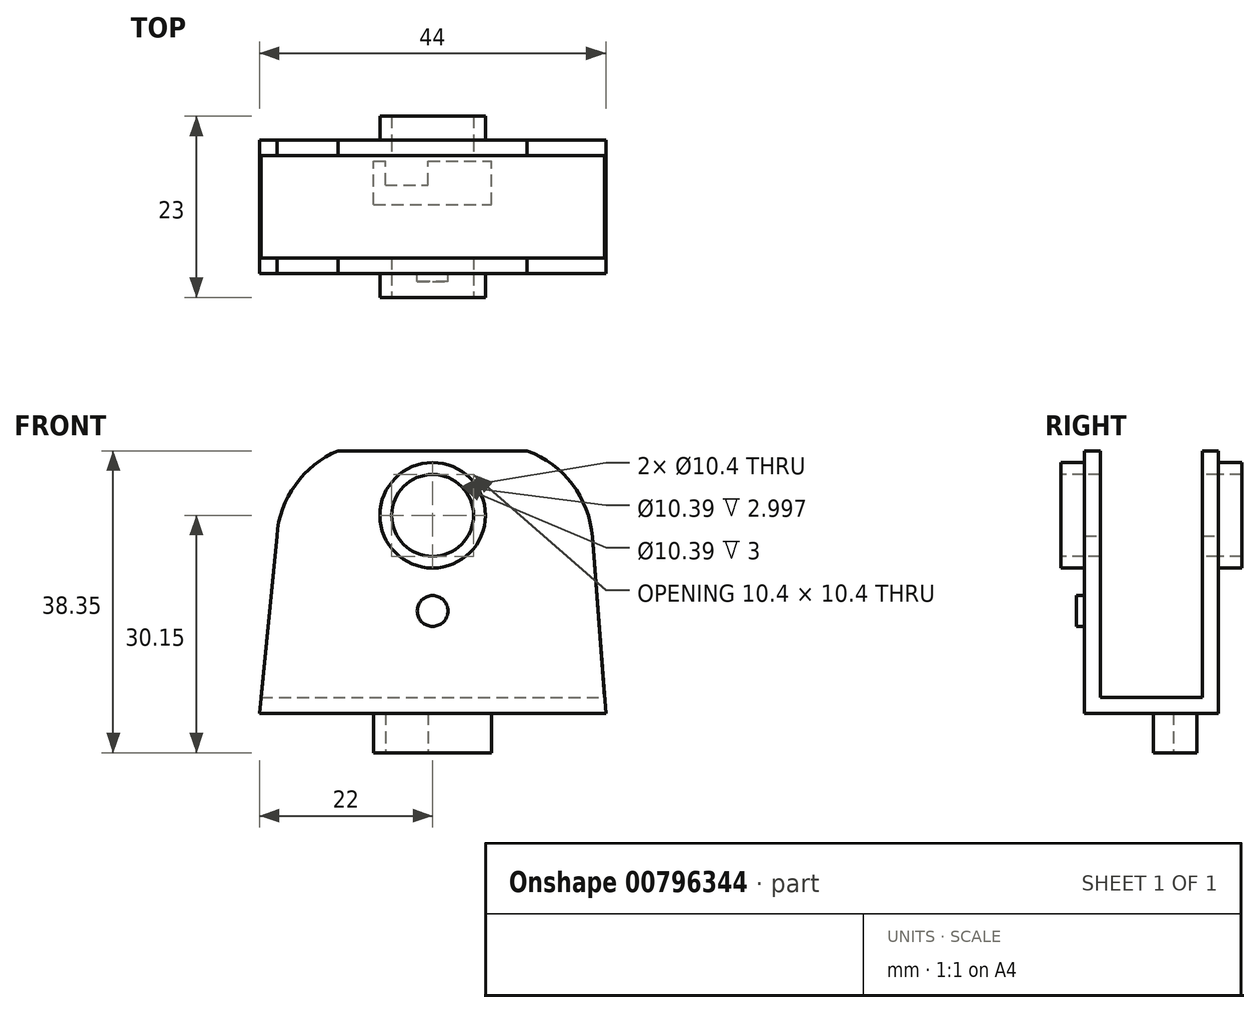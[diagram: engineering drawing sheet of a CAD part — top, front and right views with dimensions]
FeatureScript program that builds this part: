
annotation { "Feature Type Name" : "Feature", "Feature Type Description" : "" }
export const myFeature = defineFeature(function(context is Context, id is Id, definition is map)
    precondition{}
    {
        {
            var Q0;
            Q0=qCreatedBy(makeId("Front.planeOp"),FACE);
            var sketch = newSketch(context, id + "F0", { "sketchPlane" : qUnion([Q0])});
            skLineSegment(sketch, "E0", {"start": v(-22, 0) * mm, "end": v(22, 0) * mm});
            skLineSegment(sketch, "E1", {"start": v(22, 0) * mm, "end": v(20.28, 22.4) * mm});
            skArc(sketch, "E2", {"start": v(20.28, 22.4) * mm, "mid": v(17.75, 29.09) * mm, "end": v(12, 33.35) * mm});
            skLineSegment(sketch, "E3", {"start": v(12, 33.35) * mm, "end": v(-12, 33.35) * mm});
            skArc(sketch, "E4", {"start": v(-12, 33.35) * mm, "mid": v(-17.43, 29.04) * mm, "end": v(-19.79, 22.51) * mm});
            skLineSegment(sketch, "E5", {"start": v(-19.79, 22.51) * mm, "end": v(-22, 0) * mm});
            skSolve(sketch);
        }
        {
            var Q0;
            Q0 = qSketchRegion(id + "F0", true);
            extrude(context, id + "F1", {"entities" : qUnion([Q0]), "depth" : 17 * mm, "offsetDistance" : 25.4 * mm});
        }
        {
            var Q0;
            Q0=qCreatedBy(makeId("Right.planeOp"),FACE);
            var sketch = newSketch(context, id + "F2", { "sketchPlane" : qUnion([Q0])});
            skLineSegment(sketch, "E6.bottom", {"start": v(-15, 2) * mm, "end": v(-2, 2) * mm});
            skLineSegment(sketch, "E6.top", {"start": v(-15, 34.4) * mm, "end": v(-2, 34.4) * mm});
            skLineSegment(sketch, "E6.left", {"start": v(-15, 2) * mm, "end": v(-15, 34.4) * mm});
            skLineSegment(sketch, "E6.right", {"start": v(-2, 2) * mm, "end": v(-2, 34.4) * mm});
            skSolve(sketch);
        }
        {
            var Q0;
            Q0=makeQuery(id+"F2.imprint","IMPRINT",FACE,{"disambiguationData":[TD([[makeQuery(id+"F2.imprint","IMPRINT",EDGE,{"derivedFrom":sQuery(id+"F2.wireOp",EDGE,"E6.bottom")}),1.0]])]});
            extrude(context, id + "F3", {"entities" : qUnion([Q0]), "operationType" : NewBodyOperationType.REMOVE, "endBound" : BoundingType.SYMMETRIC, "oppositeDirection" : true, "depth" : 127 * mm, "offsetDistance" : 25.4 * mm});
        }
        {
            var Q0;
            Q0=makeQuery(id+"F1.opExtrude","CAP_FACE",FACE,{"disambiguationData":[OSD([sQuery(id+"F0.wireOp",EDGE,"E0"),sQuery(id+"F0.wireOp",EDGE,"E1"),sQuery(id+"F0.wireOp",EDGE,"E2"),sQuery(id+"F0.wireOp",EDGE,"E3"),sQuery(id+"F0.wireOp",EDGE,"E4"),sQuery(id+"F0.wireOp",EDGE,"E5")])],"isStart":false});
            var sketch = newSketch(context, id + "F4", { "sketchPlane" : qUnion([Q0])});
            skCircle(sketch, "E7", {"center": v(0, 25.15) * mm, "radius": 5.2 * mm});
            skSolve(sketch);
        }
        {
            var Q0;
            Q0 = qSketchRegion(id + "F4", true);
            extrude(context, id + "F5", {"entities" : qUnion([Q0]), "operationType" : NewBodyOperationType.REMOVE, "endBound" : BoundingType.THROUGH_ALL, "oppositeDirection" : true, "depth" : 25.4 * mm, "offsetDistance" : 25.4 * mm});
        }
        {
            var Q0;
            Q0=makeQuery(id+"F1.opExtrude","CAP_FACE",FACE,{"disambiguationData":[OSD([sQuery(id+"F0.wireOp",EDGE,"E0"),sQuery(id+"F0.wireOp",EDGE,"E1"),sQuery(id+"F0.wireOp",EDGE,"E2"),sQuery(id+"F0.wireOp",EDGE,"E3"),sQuery(id+"F0.wireOp",EDGE,"E4"),sQuery(id+"F0.wireOp",EDGE,"E5")])],"isStart":false});
            var sketch = newSketch(context, id + "F6", { "sketchPlane" : qUnion([Q0])});
            skCircle(sketch, "E8", {"center": v(0, 25.15) * mm, "radius": 6.7 * mm});
            skSolve(sketch);
        }
        {
            var Q0;
            Q0 = qSketchRegion(id + "F6", true);
            extrude(context, id + "F7", {"entities" : qUnion([Q0]), "operationType" : NewBodyOperationType.ADD, "depth" : 3 * mm, "offsetDistance" : 25.4 * mm});
        }
        {
            var Q0;
            Q0=makeQuery(id+"F1.opExtrude","CAP_FACE",FACE,{"disambiguationData":[OSD([sQuery(id+"F0.wireOp",EDGE,"E0"),sQuery(id+"F0.wireOp",EDGE,"E1"),sQuery(id+"F0.wireOp",EDGE,"E2"),sQuery(id+"F0.wireOp",EDGE,"E3"),sQuery(id+"F0.wireOp",EDGE,"E4"),sQuery(id+"F0.wireOp",EDGE,"E5")])],"isStart":true});
            var sketch = newSketch(context, id + "F8", { "sketchPlane" : qUnion([Q0])});
            skCircle(sketch, "E9", {"center": v(0, 25.15) * mm, "radius": 6.7 * mm});
            skSolve(sketch);
        }
        {
            var Q0;
            Q0 = qSketchRegion(id + "F8", true);
            extrude(context, id + "F9", {"entities" : qUnion([Q0]), "operationType" : NewBodyOperationType.ADD, "depth" : 3 * mm, "offsetDistance" : 25.4 * mm});
        }
        {
            var Q0;
            Q0=makeQuery(id+"F7.opExtrude","CAP_FACE",FACE,{"disambiguationData":[OSD([sQuery(id+"F6.wireOp",EDGE,"E8")])],"isStart":false});
            var sketch = newSketch(context, id + "F10", { "sketchPlane" : qUnion([Q0])});
            skCircle(sketch, "E10", {"center": v(0, 25.15) * mm, "radius": 5.2 * mm});
            skSolve(sketch);
        }
        {
            var Q0;
            Q0 = qSketchRegion(id + "F10", true);
            extrude(context, id + "F11", {"entities" : qUnion([Q0]), "operationType" : NewBodyOperationType.REMOVE, "endBound" : BoundingType.THROUGH_ALL, "oppositeDirection" : true, "depth" : 25.4 * mm, "offsetDistance" : 25.4 * mm});
        }
        {
            var Q0;
            Q0=makeQuery(id+"F1.opExtrude","SWEPT_FACE",FACE,{"disambiguationData":[OSD([sQuery(id+"F0.wireOp",EDGE,"E0")])]});
            var sketch = newSketch(context, id + "F12", { "sketchPlane" : qUnion([Q0])});
            skLineSegment(sketch, "E11.bottom", {"start": v(-7.5, 8.22) * mm, "end": v(7.5, 8.22) * mm});
            skLineSegment(sketch, "E11.top", {"start": v(-7.5, 2.72) * mm, "end": v(7.5, 2.72) * mm});
            skLineSegment(sketch, "E11.left", {"start": v(-7.5, 8.22) * mm, "end": v(-7.5, 2.72) * mm});
            skLineSegment(sketch, "E11.right", {"start": v(7.5, 8.22) * mm, "end": v(7.5, 2.72) * mm});
            skSolve(sketch);
        }
        {
            var Q0;
            Q0 = qSketchRegion(id + "F12", true);
            extrude(context, id + "F13", {"entities" : qUnion([Q0]), "operationType" : NewBodyOperationType.ADD, "depth" : 5 * mm, "offsetDistance" : 25.4 * mm});
        }
        {
            var Q0;
            Q0=makeQuery(id+"F13.opExtrude","CAP_FACE",FACE,{"disambiguationData":[OSD([sQuery(id+"F12.wireOp",EDGE,"E11.bottom"),sQuery(id+"F12.wireOp",EDGE,"E11.top"),sQuery(id+"F12.wireOp",EDGE,"E11.left"),sQuery(id+"F12.wireOp",EDGE,"E11.right")])],"isStart":false});
            var sketch = newSketch(context, id + "F14", { "sketchPlane" : qUnion([Q0])});
            skLineSegment(sketch, "E12.bottom", {"start": v(-6, 5.72) * mm, "end": v(-0.58, 5.72) * mm});
            skLineSegment(sketch, "E12.top", {"start": v(-6, 1.4) * mm, "end": v(-0.58, 1.4) * mm});
            skLineSegment(sketch, "E12.left", {"start": v(-6, 5.72) * mm, "end": v(-6, 1.4) * mm});
            skLineSegment(sketch, "E12.right", {"start": v(-0.58, 5.72) * mm, "end": v(-0.58, 1.4) * mm});
            skSolve(sketch);
        }
        {
            var Q0;
            Q0 = qSketchRegion(id + "F14", true);
            var Q1;
            Q1=makeQuery(id+"F1.opExtrude","SWEPT_FACE",FACE,{"disambiguationData":[OSD([sQuery(id+"F0.wireOp",EDGE,"E0")])]});
            extrude(context, id + "F15", {"entities" : qUnion([Q0]), "operationType" : NewBodyOperationType.REMOVE, "endBound" : BoundingType.UP_TO_SURFACE, "oppositeDirection" : true, "depth" : 25.4 * mm, "endBoundEntityFace" : qUnion([Q1]), "offsetDistance" : 25.4 * mm});
        }
        {
            var Q0;
            Q0=makeQuery(id+"F1.opExtrude","CAP_FACE",FACE,{"disambiguationData":[OSD([sQuery(id+"F0.wireOp",EDGE,"E0"),sQuery(id+"F0.wireOp",EDGE,"E1"),sQuery(id+"F0.wireOp",EDGE,"E2"),sQuery(id+"F0.wireOp",EDGE,"E3"),sQuery(id+"F0.wireOp",EDGE,"E4"),sQuery(id+"F0.wireOp",EDGE,"E5")])],"isStart":false});
            var sketch = newSketch(context, id + "F16", { "sketchPlane" : qUnion([Q0])});
            skCircle(sketch, "E13", {"center": v(0, 13) * mm, "radius": 1.95 * mm});
            skSolve(sketch);
        }
        {
            var Q0;
            Q0 = qSketchRegion(id + "F16", true);
            extrude(context, id + "F17", {"entities" : qUnion([Q0]), "operationType" : NewBodyOperationType.ADD, "depth" : 1 * mm, "offsetDistance" : 25.4 * mm});
        }
    });
